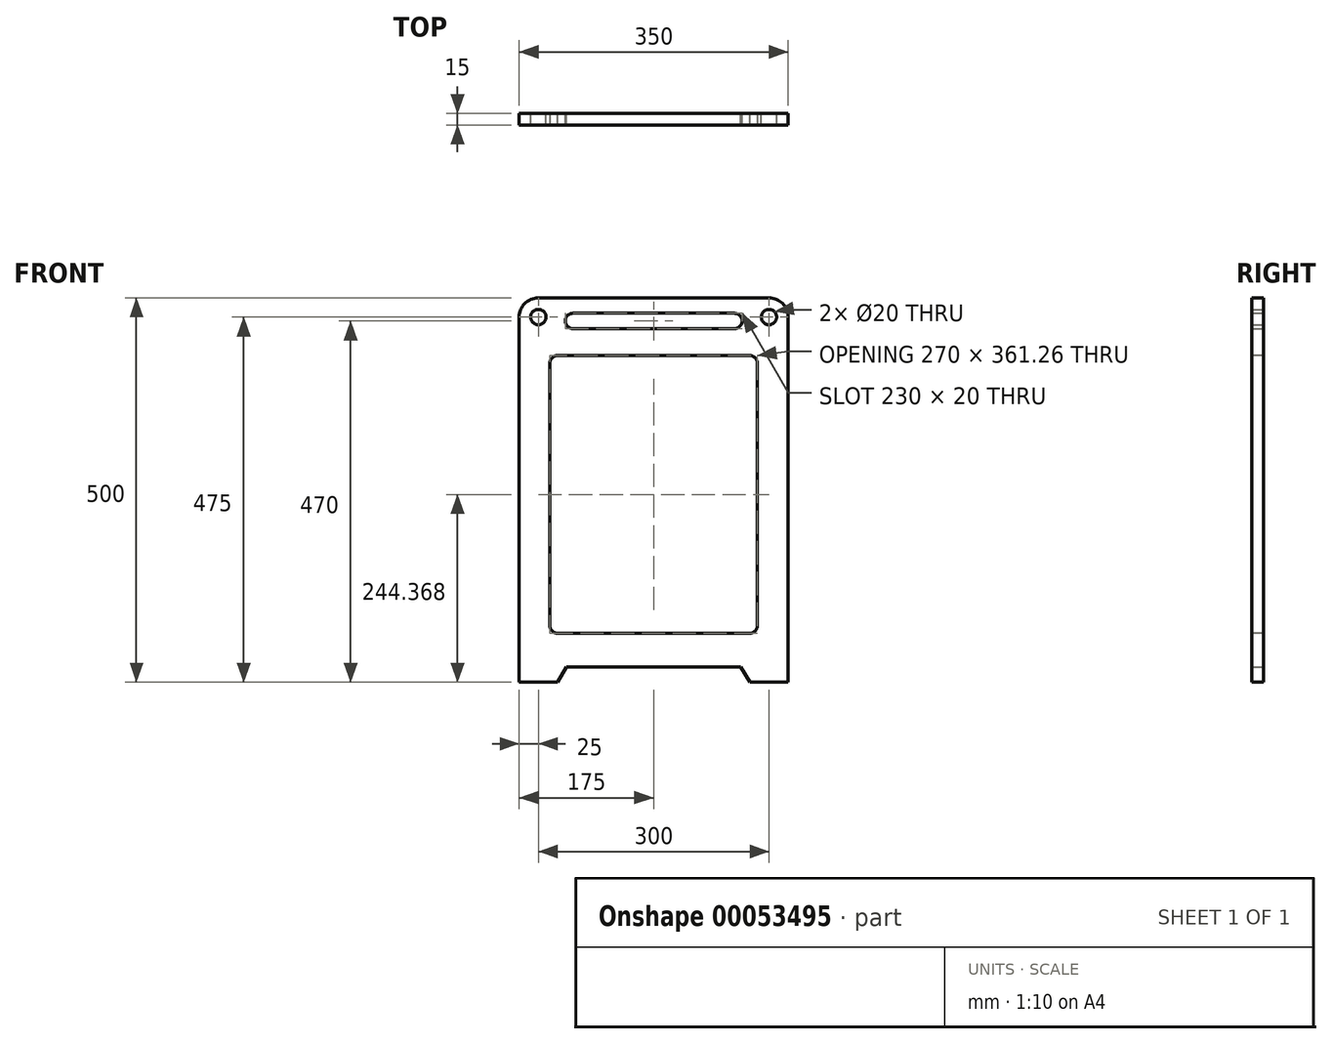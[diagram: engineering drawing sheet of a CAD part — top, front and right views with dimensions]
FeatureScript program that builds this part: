
annotation { "Feature Type Name" : "Feature", "Feature Type Description" : "" }
export const myFeature = defineFeature(function(context is Context, id is Id, definition is map)
    precondition{}
    {
        {
            var Q0;
            Q0=qCreatedBy(makeId("Front.planeOp"),FACE);
            var sketch = newSketch(context, id + "F0", { "sketchPlane" : qUnion([Q0])});
            skLineSegment(sketch, "E0.rect.bottom", {"start": v(-150, 250) * mm, "end": v(150, 250) * mm});
            skLineSegment(sketch, "E0.rect.top", {"start": v(-175, -250) * mm, "end": v(175, -250) * mm, "construction": true});
            skLineSegment(sketch, "E0.rect.left", {"start": v(-175, 225) * mm, "end": v(-175, -250) * mm});
            skLineSegment(sketch, "E0.rect.right", {"start": v(175, 225) * mm, "end": v(175, -250) * mm});
            skPoint(sketch, "E0.rect.middle", {"position": v(0, 0) * mm});
            skLineSegment(sketch, "E1", {"start": v(-125, -250) * mm, "end": v(-113.45, -230) * mm});
            skLineSegment(sketch, "E2", {"start": v(-113.45, -230) * mm, "end": v(0, -230) * mm});
            skLineSegment(sketch, "E3", {"start": v(0, -230) * mm, "end": v(0, -250) * mm, "construction": true});
            skLineSegment(sketch, "E4", {"start": v(-125, -250) * mm, "end": v(-175, -250) * mm});
            skLineSegment(sketch, "E5.MirrorCS", {"start": v(125, -250) * mm, "end": v(113.45, -230) * mm});
            skLineSegment(sketch, "E6.MirrorCS", {"start": v(113.45, -230) * mm, "end": v(0, -230) * mm});
            skLineSegment(sketch, "E7", {"start": v(125, -250) * mm, "end": v(175, -250) * mm});
            skLineSegment(sketch, "E8", {"start": v(-105, 220) * mm, "end": v(105, 220) * mm, "construction": true});
            skArc(sketch, "E9.0.startCap", {"start": v(-105, 210) * mm, "mid": v(-115, 220) * mm, "end": v(-105, 230) * mm});
            skArc(sketch, "E9.0.endCap", {"start": v(105, 230) * mm, "mid": v(115, 220) * mm, "end": v(105, 210) * mm});
            skLineSegment(sketch, "E9.0.left", {"start": v(-105, 230) * mm, "end": v(105, 230) * mm});
            skLineSegment(sketch, "E9.0.right", {"start": v(-105, 210) * mm, "end": v(105, 210) * mm});
            skPoint(sketch, "E10.visualSharp", {"position": v(-175, 250) * mm});
            skArc(sketch, "E10.filletArc", {"start": v(-150, 250) * mm, "mid": v(-167.68, 242.68) * mm, "end": v(-175, 225) * mm});
            skPoint(sketch, "E11.visualSharp", {"position": v(175, 250) * mm});
            skArc(sketch, "E11.filletArc", {"start": v(175, 225) * mm, "mid": v(167.68, 242.68) * mm, "end": v(150, 250) * mm});
            skLineSegment(sketch, "E12", {"start": v(0, 220) * mm, "end": v(0, 0) * mm, "construction": true});
            skCircle(sketch, "E13", {"center": v(-150, 225) * mm, "radius": 10 * mm});
            skCircle(sketch, "E14.MirrorC", {"center": v(150, 225) * mm, "radius": 10 * mm});
            skSolve(sketch);
        }
        {
            var Q0;
            Q0 = qSketchRegion(id + "F0", true);
            extrude(context, id + "F1", {"entities" : qUnion([Q0]), "depth" : 15 * mm});
        }
        {
            var Q0;
            Q0=makeQuery(id+"F1.opExtrude","CAP_FACE",FACE,{"disambiguationData":[OSD([sQuery(id+"F0.wireOp",EDGE,"E0.rect.bottom"),sQuery(id+"F0.wireOp",EDGE,"E0.rect.left"),sQuery(id+"F0.wireOp",EDGE,"E0.rect.right"),sQuery(id+"F0.wireOp",EDGE,"E1"),sQuery(id+"F0.wireOp",EDGE,"E2"),sQuery(id+"F0.wireOp",EDGE,"E4"),sQuery(id+"F0.wireOp",EDGE,"E5.MirrorCS"),sQuery(id+"F0.wireOp",EDGE,"E6.MirrorCS"),sQuery(id+"F0.wireOp",EDGE,"E7"),sQuery(id+"F0.wireOp",EDGE,"E9.0.startCap"),sQuery(id+"F0.wireOp",EDGE,"E9.0.endCap"),sQuery(id+"F0.wireOp",EDGE,"E9.0.left"),sQuery(id+"F0.wireOp",EDGE,"E9.0.right"),sQuery(id+"F0.wireOp",EDGE,"E10.filletArc"),sQuery(id+"F0.wireOp",EDGE,"E11.filletArc"),sQuery(id+"F0.wireOp",EDGE,"E13"),sQuery(id+"F0.wireOp",EDGE,"E14.MirrorC")])],"isStart":false});
            var sketch = newSketch(context, id + "F2", { "sketchPlane" : qUnion([Q0])});
            skLineSegment(sketch, "E15.rect.bottom", {"start": v(125, 175) * mm, "end": v(-125, 175) * mm});
            skLineSegment(sketch, "E15.rect.top", {"start": v(125, -186.26) * mm, "end": v(-125, -186.26) * mm});
            skLineSegment(sketch, "E15.rect.left", {"start": v(135, 165) * mm, "end": v(135, -176.26) * mm});
            skLineSegment(sketch, "E15.rect.right", {"start": v(-135, 165) * mm, "end": v(-135, -176.26) * mm});
            skPoint(sketch, "E15.rect.middle", {"position": v(0, -5.63) * mm});
            skPoint(sketch, "E16.visualSharp", {"position": v(-135, 175) * mm});
            skArc(sketch, "E16.filletArc", {"start": v(-125, 175) * mm, "mid": v(-132.07, 172.07) * mm, "end": v(-135, 165) * mm});
            skPoint(sketch, "E17.visualSharp", {"position": v(135, 175) * mm});
            skArc(sketch, "E17.filletArc", {"start": v(135, 165) * mm, "mid": v(132.07, 172.07) * mm, "end": v(125, 175) * mm});
            skPoint(sketch, "E18.visualSharp", {"position": v(-135, -186.26) * mm});
            skArc(sketch, "E18.filletArc", {"start": v(-135, -176.26) * mm, "mid": v(-132.07, -183.34) * mm, "end": v(-125, -186.26) * mm});
            skPoint(sketch, "E19.visualSharp", {"position": v(135, -186.26) * mm});
            skArc(sketch, "E19.filletArc", {"start": v(125, -186.26) * mm, "mid": v(132.07, -183.34) * mm, "end": v(135, -176.26) * mm});
            skSolve(sketch);
        }
        {
            var Q0;
            Q0 = qSketchRegion(id + "F2", true);
            extrude(context, id + "F3", {"entities" : qUnion([Q0]), "operationType" : NewBodyOperationType.REMOVE, "endBound" : BoundingType.THROUGH_ALL, "oppositeDirection" : true, "depth" : 25 * mm});
        }
    });
